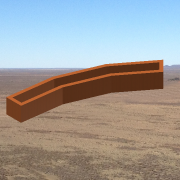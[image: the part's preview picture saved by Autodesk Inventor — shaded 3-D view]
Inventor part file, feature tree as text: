
AUTODESK INVENTOR PART (.ipt)
format: ipt  version: 2013 SP2 (Build 170200200, 200)  size: 148,992 bytes
history: native  units: in
note: dims shown in document units (in); Inventor stores cm internally (conversion verified against a paired STEP export)
features: extrude x2, sketch x2
ambient origin geometry x8: Origin, YZ Plane, XZ Plane, XY Plane, X Axis, Y Axis, Z Axis, Center Point
bodies: Solid1 (feature_tree)
feature tree (4):
  extrude  "Extrusion1"  Depth=14.0in
  extrude  "Extrusion2"  Depth=3.5in
  sketch  "Sketch3"  dims[d20=192.0in d21=14.0in]
  sketch  "Sketch4"  dims[d22=18.0in d23=0.0in d24=3.5in d25=18.0in d26=16.0in d27=0.0in]
